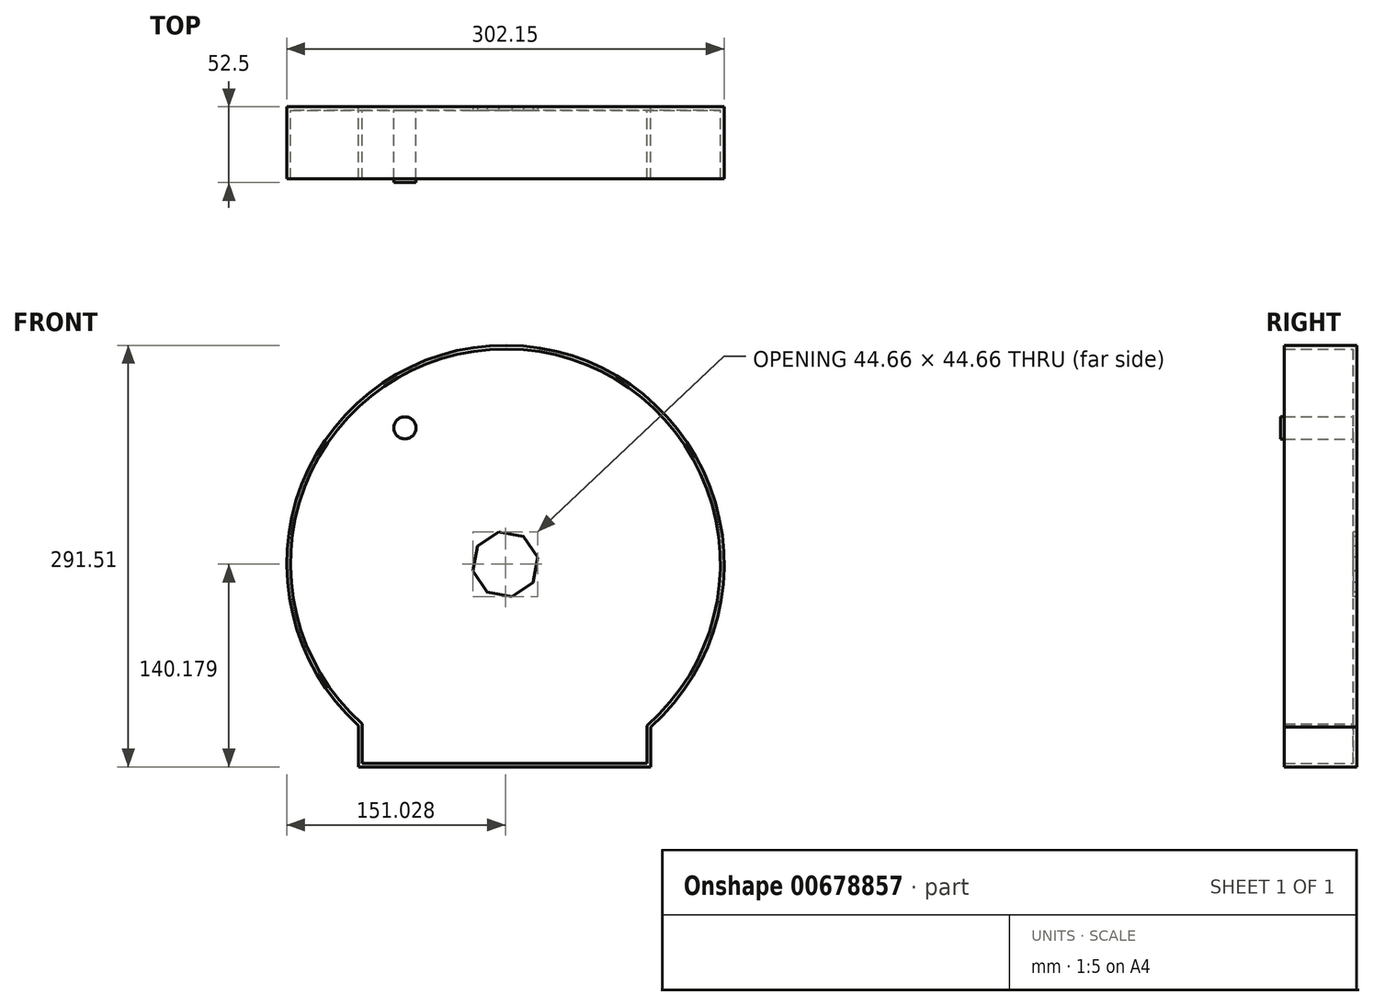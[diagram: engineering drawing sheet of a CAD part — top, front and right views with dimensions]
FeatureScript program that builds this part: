
annotation { "Feature Type Name" : "Feature", "Feature Type Description" : "" }
export const myFeature = defineFeature(function(context is Context, id is Id, definition is map)
    precondition{}
    {
        {
            var Q0;
            Q0=qCreatedBy(makeId("Front.planeOp"),FACE);
            var sketch = newSketch(context, id + "F0", { "sketchPlane" : qUnion([Q0])});
            skCircle(sketch, "E0", {"center": v(0, 0) * mm, "radius": 53.72 * mm});
            skCircle(sketch, "E1", {"center": v(0, 0) * mm, "radius": 58.67 * mm, "construction": true});
            skCircle(sketch, "E2", {"center": v(0, 0) * mm, "radius": 63.5 * mm, "construction": true});
            skLineSegment(sketch, "E3", {"start": v(0, 0) * mm, "end": v(0, 97.8) * mm, "construction": true});
            skLineSegment(sketch, "E4", {"start": v(0, 0) * mm, "end": v(-6.4, 97.8) * mm, "construction": true});
            skLineSegment(sketch, "E5", {"start": v(0, 58.67) * mm, "end": v(-71.5, 58.67) * mm, "construction": true});
            skLineSegment(sketch, "E6", {"start": v(0, 58.67) * mm, "end": v(-73, 32.1) * mm, "construction": true});
            skCircle(sketch, "E7", {"center": v(0, 0) * mm, "radius": 55.14 * mm, "construction": true});
            skCircle(sketch, "E8", {"center": v(0, 58.67) * mm, "radius": 14.6 * mm, "construction": true});
            skCircle(sketch, "E9", {"center": v(-13.72, 53.68) * mm, "radius": 14.6 * mm, "construction": true});
            skArc(sketch, "E10", {"start": v(0, 58.67) * mm, "mid": v(-1.2, 61.19) * mm, "end": v(-2.86, 63.44) * mm});
            skArc(sketch, "E11", {"start": v(0.88, 53.71) * mm, "mid": v(0.7, 56.24) * mm, "end": v(0, 58.67) * mm});
            skArc(sketch, "E12.MirrorCS", {"start": v(-7.66, 58.17) * mm, "mid": v(-6.8, 60.82) * mm, "end": v(-5.45, 63.27) * mm});
            skArc(sketch, "E13.MirrorCS", {"start": v(-7.88, 53.14) * mm, "mid": v(-8.03, 55.67) * mm, "end": v(-7.66, 58.17) * mm});
            skArc(sketch, "E14", {"start": v(-5.45, 63.27) * mm, "mid": v(-4.08, 62.24) * mm, "end": v(-2.86, 63.44) * mm});
            skCircle(sketch, "E15", {"center": v(0, 0) * mm, "radius": 38.1 * mm});
            skCircle(sketch, "E16.cCircle", {"center": v(0, 0) * mm, "radius": 21.09 * mm, "construction": true});
            skLineSegment(sketch, "E16.0", {"start": v(19.13, -12.45) * mm, "end": v(4.73, -22.33) * mm});
            skLineSegment(sketch, "E16.1", {"start": v(4.73, -22.33) * mm, "end": v(-12.45, -19.13) * mm});
            skLineSegment(sketch, "E16.2", {"start": v(-12.45, -19.13) * mm, "end": v(-22.33, -4.73) * mm});
            skLineSegment(sketch, "E16.3", {"start": v(-22.33, -4.73) * mm, "end": v(-19.13, 12.45) * mm});
            skLineSegment(sketch, "E16.4", {"start": v(-19.13, 12.45) * mm, "end": v(-4.73, 22.33) * mm});
            skLineSegment(sketch, "E16.5", {"start": v(-4.73, 22.33) * mm, "end": v(12.45, 19.13) * mm});
            skLineSegment(sketch, "E16.6", {"start": v(12.45, 19.13) * mm, "end": v(22.33, 4.73) * mm});
            skLineSegment(sketch, "E16.7", {"start": v(22.33, 4.73) * mm, "end": v(19.13, -12.45) * mm});
            skPoint(sketch, "E16.0.midPoint", {"position": v(11.93, -17.39) * mm});
            skSolve(sketch);
        }
        {
            var Q0;
            {var subQ0=sQuery(id+"F0.wireOp",EDGE,"E0");var subQ1=makeQuery(id+"F0.imprint","INTERSECT",VERTEX,{"derivedFrom":[subQ0,sQuery(id+"F0.wireOp",EDGE,"E11")]});Q0=makeQuery(id+"F0.imprint","IMPRINT",FACE,{"disambiguationData":[TD([[makeQuery(id+"F0.imprint","IMPRINT",EDGE,{"disambiguationData":[TD([[subQ1,-1.0]])],"derivedFrom":subQ0}),1.0]])]});}
            var Q1;
            Q1=makeQuery(id+"F0.imprint","IMPRINT",FACE,{"disambiguationData":[TD([[makeQuery(id+"F0.imprint","IMPRINT",EDGE,{"derivedFrom":sQuery(id+"F0.wireOp",EDGE,"E10")}),1.0]])]});
            extrude(context, id + "F1", {"entities" : qUnion([Q0, Q1]), "depth" : 25 * mm, "offsetDistance" : 25 * mm});
        }
        {
            var Q0;
            Q0=makeQuery(id+"F1.opExtrude","SWEPT_BODY",BODY,{"disambiguationData":[OSD([sQuery(id+"F0.wireOp",EDGE,"E0"),sQuery(id+"F0.wireOp",EDGE,"E10"),sQuery(id+"F0.wireOp",EDGE,"E11"),sQuery(id+"F0.wireOp",EDGE,"E12.MirrorCS"),sQuery(id+"F0.wireOp",EDGE,"E13.MirrorCS"),sQuery(id+"F0.wireOp",EDGE,"E14")])]});
            var Q1;
            Q1=makeQuery(id+"F1.opExtrude","SWEPT_FACE",FACE,{"disambiguationData":[OSD([sQuery(id+"F0.wireOp",EDGE,"E0")])]});
            circularPattern(context, id + "F2", {"entities" : qUnion([Q0]), "axis" : qUnion([Q1]), "angle" : 360 * degree, "instanceCount" : 24, "equalSpace" : true});
        }
        {
            var Q0;
            Q0=makeQuery(id+"F0.imprint","IMPRINT",FACE,{"disambiguationData":[TD([[makeQuery(id+"F0.imprint","IMPRINT",EDGE,{"derivedFrom":sQuery(id+"F0.wireOp",EDGE,"E15")}),1.0]])]});
            extrude(context, id + "F3", {"entities" : qUnion([Q0]), "operationType" : NewBodyOperationType.ADD, "depth" : 35 * mm, "offsetDistance" : 25 * mm});
        }
        {
            var Q0;
            Q0=makeQuery(id+"F3.opExtrude","CAP_FACE",FACE,{"disambiguationData":[OSD([sQuery(id+"F0.wireOp",EDGE,"E15"),sQuery(id+"F0.wireOp",EDGE,"E16.0"),sQuery(id+"F0.wireOp",EDGE,"E16.1"),sQuery(id+"F0.wireOp",EDGE,"E16.2"),sQuery(id+"F0.wireOp",EDGE,"E16.3"),sQuery(id+"F0.wireOp",EDGE,"E16.4"),sQuery(id+"F0.wireOp",EDGE,"E16.5"),sQuery(id+"F0.wireOp",EDGE,"E16.6"),sQuery(id+"F0.wireOp",EDGE,"E16.7")])],"isStart":false});
            fillet(context, id + "F4", {"entities" : qUnion([Q0]), "radius" : 5 * mm, "tangentPropagation" : true, "allowEdgeOverflow" : false});
        }
        {
            var Q0;
            Q0=makeQuery(id+"F3.opExtrude","CAP_FACE",FACE,{"disambiguationData":[OSD([sQuery(id+"F0.wireOp",EDGE,"E15"),sQuery(id+"F0.wireOp",EDGE,"E16.0"),sQuery(id+"F0.wireOp",EDGE,"E16.1"),sQuery(id+"F0.wireOp",EDGE,"E16.2"),sQuery(id+"F0.wireOp",EDGE,"E16.3"),sQuery(id+"F0.wireOp",EDGE,"E16.4"),sQuery(id+"F0.wireOp",EDGE,"E16.5"),sQuery(id+"F0.wireOp",EDGE,"E16.6"),sQuery(id+"F0.wireOp",EDGE,"E16.7")])],"isStart":false});
            var Q1;
            Q1=makeQuery(id+"F4.opFillet","BLEND_FACE",FACE,{"disambiguationData":[OSD([sQuery(id+"F0.wireOp",EDGE,"E15")])]});
            var Q2;
            Q2=makeQuery(id+"F4.opFillet","BLEND_FACE",FACE,{"disambiguationData":[OSD([sQuery(id+"F0.wireOp",EDGE,"E16.3")])]});
            var Q3;
            Q3=makeQuery(id+"F4.opFillet","BLEND_FACE",FACE,{"disambiguationData":[OSD([sQuery(id+"F0.wireOp",EDGE,"E16.4")])]});
            var Q4;
            Q4=makeQuery(id+"F4.opFillet","BLEND_FACE",FACE,{"disambiguationData":[OSD([sQuery(id+"F0.wireOp",EDGE,"E16.5")])]});
            var Q5;
            Q5=makeQuery(id+"F4.opFillet","BLEND_FACE",FACE,{"disambiguationData":[OSD([sQuery(id+"F0.wireOp",EDGE,"E16.6")])]});
            var Q6;
            Q6=makeQuery(id+"F4.opFillet","BLEND_FACE",FACE,{"disambiguationData":[OSD([sQuery(id+"F0.wireOp",EDGE,"E16.7")])]});
            var Q7;
            Q7=makeQuery(id+"F4.opFillet","BLEND_FACE",FACE,{"disambiguationData":[OSD([sQuery(id+"F0.wireOp",EDGE,"E16.0")])]});
            var Q8;
            Q8=makeQuery(id+"F4.opFillet","BLEND_FACE",FACE,{"disambiguationData":[OSD([sQuery(id+"F0.wireOp",EDGE,"E16.1")])]});
            var Q9;
            Q9=makeQuery(id+"F4.opFillet","BLEND_FACE",FACE,{"disambiguationData":[OSD([sQuery(id+"F0.wireOp",EDGE,"E16.2")])]});
            chamfer(context, id + "F5", {"entities" : qUnion([Q0, Q1, Q2, Q3, Q4, Q5, Q6, Q7, Q8, Q9]), "width" : 5 * mm, "tangentPropagation" : true});
        }
        {
            var Q0;
            Q0=qCreatedBy(makeId("Front.planeOp"),FACE);
            var sketch = newSketch(context, id + "F6", { "sketchPlane" : qUnion([Q0])});
            skLineSegment(sketch, "E17", {"start": v(-74.5, -41.52) * mm, "end": v(-74.5, -70.12) * mm});
            skLineSegment(sketch, "E18", {"start": v(-74.5, -70.12) * mm, "end": v(127.37, -70.12) * mm});
            skLineSegment(sketch, "E19", {"start": v(127.37, -70.12) * mm, "end": v(127.37, -42.65) * mm});
            skArc(sketch, "E20", {"start": v(127.37, -42.65) * mm, "mid": v(27.9, 221.38) * mm, "end": v(-74.5, -41.52) * mm});
            skSolve(sketch);
        }
        {
            var Q0;
            Q0=makeQuery(id+"F6.imprint","IMPRINT",FACE,{"disambiguationData":[TD([[makeQuery(id+"F6.imprint","IMPRINT",EDGE,{"derivedFrom":sQuery(id+"F6.wireOp",EDGE,"E17")}),1.0]])]});
            extrude(context, id + "F7", {"entities" : qUnion([Q0]), "operationType" : NewBodyOperationType.ADD, "depth" : 50 * mm, "offsetDistance" : 25 * mm});
        }
        {
            var Q0;
            Q0=makeQuery(id+"F7.opExtrude","CAP_FACE",FACE,{"disambiguationData":[OSD([sQuery(id+"F6.wireOp",EDGE,"E17"),sQuery(id+"F6.wireOp",EDGE,"E18"),sQuery(id+"F6.wireOp",EDGE,"E19"),sQuery(id+"F6.wireOp",EDGE,"E20")])],"isStart":false});
            shell(context, id + "F8", {"entities" : qUnion([Q0]), "thickness" : 2.5 * mm});
        }
        {
            var Q0;
            Q0=makeQuery(id+"F8.opShell","OFFSET_FACE",FACE,{"disambiguationData":[OSD([sQuery(id+"F0.wireOp",EDGE,"E0"),sQuery(id+"F0.wireOp",EDGE,"E10"),sQuery(id+"F0.wireOp",EDGE,"E11"),sQuery(id+"F0.wireOp",EDGE,"E12.MirrorCS"),sQuery(id+"F0.wireOp",EDGE,"E13.MirrorCS"),sQuery(id+"F0.wireOp",EDGE,"E14"),sQuery(id+"F0.wireOp",EDGE,"E15"),sQuery(id+"F0.wireOp",EDGE,"E16.0"),sQuery(id+"F0.wireOp",EDGE,"E16.1"),sQuery(id+"F0.wireOp",EDGE,"E16.2"),sQuery(id+"F0.wireOp",EDGE,"E16.3"),sQuery(id+"F0.wireOp",EDGE,"E16.4"),sQuery(id+"F0.wireOp",EDGE,"E16.5"),sQuery(id+"F0.wireOp",EDGE,"E16.6"),sQuery(id+"F0.wireOp",EDGE,"E16.7"),sQuery(id+"F6.wireOp",EDGE,"E17"),sQuery(id+"F6.wireOp",EDGE,"E18"),sQuery(id+"F6.wireOp",EDGE,"E19"),sQuery(id+"F6.wireOp",EDGE,"E20")])]});
            var sketch = newSketch(context, id + "F9", { "sketchPlane" : qUnion([Q0])});
            skCircle(sketch, "E21.cCircle", {"center": v(27.02, 70.06) * mm, "radius": 21.09 * mm, "construction": true});
            skLineSegment(sketch, "E21.0", {"start": v(46.15, 57.61) * mm, "end": v(31.74, 47.73) * mm});
            skLineSegment(sketch, "E21.1", {"start": v(31.74, 47.73) * mm, "end": v(14.57, 50.93) * mm});
            skLineSegment(sketch, "E21.2", {"start": v(14.57, 50.93) * mm, "end": v(4.69, 65.33) * mm});
            skLineSegment(sketch, "E21.3", {"start": v(4.69, 65.33) * mm, "end": v(7.89, 82.5) * mm});
            skLineSegment(sketch, "E21.4", {"start": v(7.89, 82.5) * mm, "end": v(22.3, 92.39) * mm});
            skLineSegment(sketch, "E21.5", {"start": v(22.3, 92.39) * mm, "end": v(39.47, 89.19) * mm});
            skLineSegment(sketch, "E21.6", {"start": v(39.47, 89.19) * mm, "end": v(49.35, 74.78) * mm});
            skLineSegment(sketch, "E21.7", {"start": v(49.35, 74.78) * mm, "end": v(46.15, 57.61) * mm});
            skSolve(sketch);
        }
        {
            var Q0;
            Q0=makeQuery(id+"F9.imprint","IMPRINT",FACE,{"disambiguationData":[TD([[makeQuery(id+"F9.imprint","IMPRINT",EDGE,{"derivedFrom":sQuery(id+"F9.wireOp",EDGE,"E21.0")}),-1.0]])]});
            extrude(context, id + "F10", {"entities" : qUnion([Q0]), "operationType" : NewBodyOperationType.REMOVE, "oppositeDirection" : true, "depth" : 25 * mm, "offsetDistance" : 25 * mm});
        }
        {
            var Q0;
            Q0=makeQuery(id+"F8.opShell","OFFSET_FACE",FACE,{"disambiguationData":[OSD([sQuery(id+"F0.wireOp",EDGE,"E0"),sQuery(id+"F0.wireOp",EDGE,"E10"),sQuery(id+"F0.wireOp",EDGE,"E11"),sQuery(id+"F0.wireOp",EDGE,"E12.MirrorCS"),sQuery(id+"F0.wireOp",EDGE,"E13.MirrorCS"),sQuery(id+"F0.wireOp",EDGE,"E14"),sQuery(id+"F0.wireOp",EDGE,"E15"),sQuery(id+"F0.wireOp",EDGE,"E16.0"),sQuery(id+"F0.wireOp",EDGE,"E16.1"),sQuery(id+"F0.wireOp",EDGE,"E16.2"),sQuery(id+"F0.wireOp",EDGE,"E16.3"),sQuery(id+"F0.wireOp",EDGE,"E16.4"),sQuery(id+"F0.wireOp",EDGE,"E16.5"),sQuery(id+"F0.wireOp",EDGE,"E16.6"),sQuery(id+"F0.wireOp",EDGE,"E16.7"),sQuery(id+"F6.wireOp",EDGE,"E17"),sQuery(id+"F6.wireOp",EDGE,"E18"),sQuery(id+"F6.wireOp",EDGE,"E19"),sQuery(id+"F6.wireOp",EDGE,"E20")])]});
            var sketch = newSketch(context, id + "F11", { "sketchPlane" : qUnion([Q0])});
            skCircle(sketch, "E22", {"center": v(-42.4, 164.3) * mm, "radius": 7.65 * mm});
            skSolve(sketch);
        }
        {
            var Q0;
            Q0=makeQuery(id+"F11.imprint","IMPRINT",FACE,{"disambiguationData":[TD([[makeQuery(id+"F11.imprint","IMPRINT",EDGE,{"derivedFrom":sQuery(id+"F11.wireOp",EDGE,"E22")}),1.0]])]});
            extrude(context, id + "F12", {"entities" : qUnion([Q0]), "operationType" : NewBodyOperationType.ADD, "depth" : 50 * mm, "offsetDistance" : 25 * mm});
        }
    });
